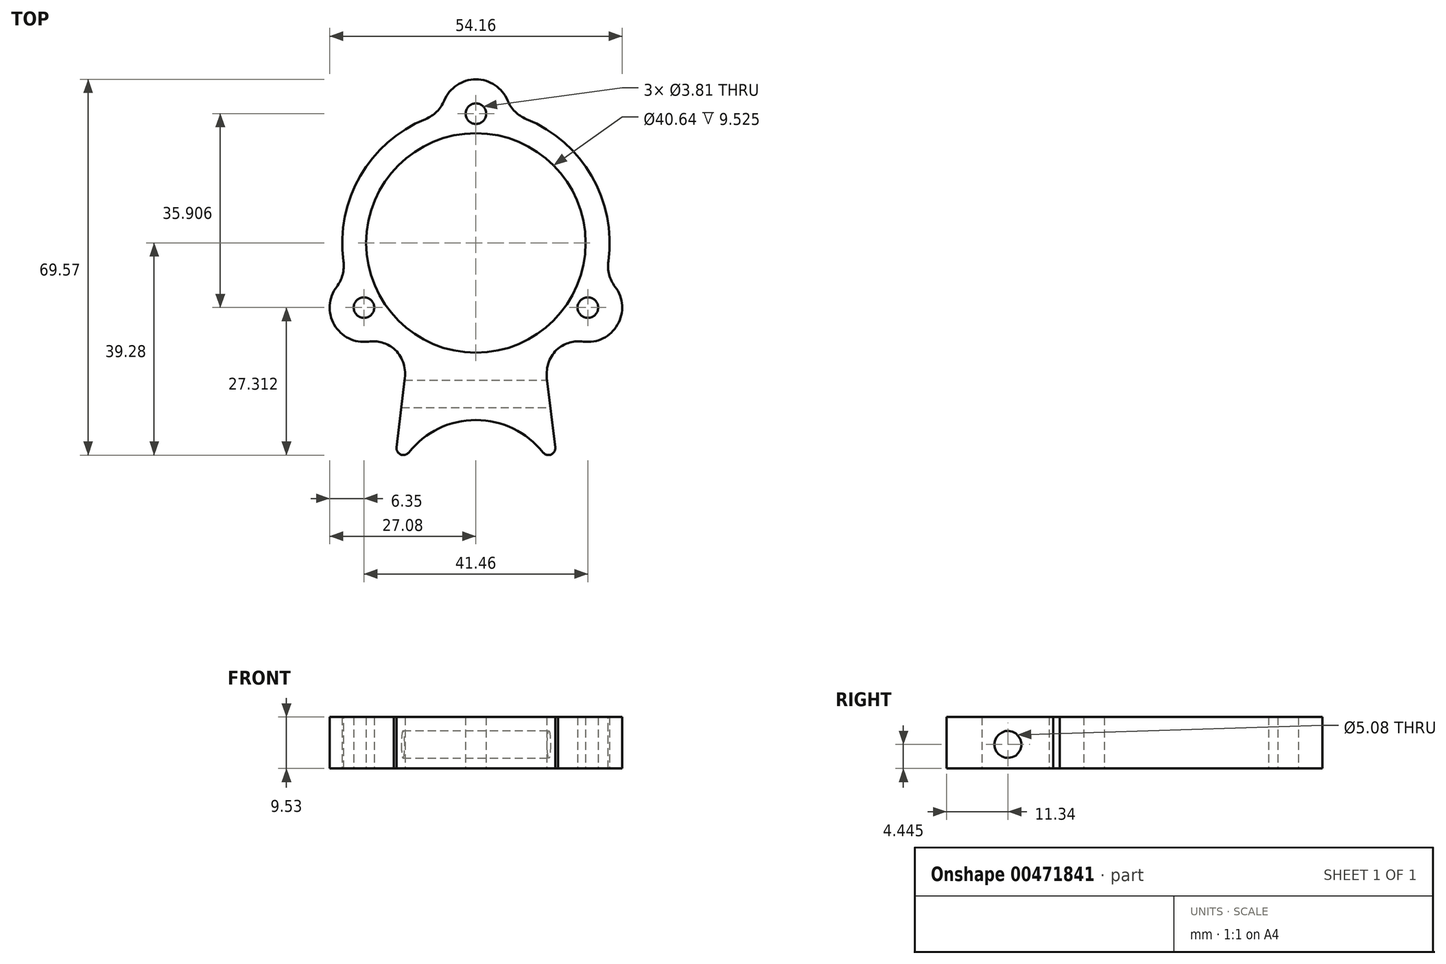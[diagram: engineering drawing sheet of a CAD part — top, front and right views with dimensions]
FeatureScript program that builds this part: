
annotation { "Feature Type Name" : "Feature", "Feature Type Description" : "" }
export const myFeature = defineFeature(function(context is Context, id is Id, definition is map)
    precondition{}
    {
        {
            var Q0;
            Q0=qCreatedBy(makeId("Top.planeOp"),FACE);
            var sketch = newSketch(context, id + "F0", { "sketchPlane" : qUnion([Q0])});
            skCircle(sketch, "E0", {"center": v(0, 0) * mm, "radius": 20.32 * mm});
            skCircle(sketch, "E1", {"center": v(0, 0) * mm, "radius": 24.77 * mm});
            skLineSegment(sketch, "E2", {"start": v(0, 0) * mm, "end": v(0, 42.77) * mm, "construction": true});
            skLineSegment(sketch, "E3", {"start": v(0, 0) * mm, "end": v(-43.71, -25.24) * mm, "construction": true});
            skLineSegment(sketch, "E4", {"start": v(0, 0) * mm, "end": v(46.9, -27.08) * mm, "construction": true});
            skLineSegment(sketch, "E5", {"start": v(-6.35, 2.16) * mm, "end": v(-6.35, 48.97) * mm, "construction": true});
            skLineSegment(sketch, "E6.MirrorCS", {"start": v(6.35, 2.16) * mm, "end": v(6.35, 48.97) * mm, "construction": true});
            skLineSegment(sketch, "E7", {"start": v(-11.23, 0.85) * mm, "end": v(-48.99, -20.95) * mm, "construction": true});
            skLineSegment(sketch, "E8.MirrorCS", {"start": v(-4.88, -10.15) * mm, "end": v(-42.64, -31.95) * mm, "construction": true});
            skLineSegment(sketch, "E9", {"start": v(0.14, -7.41) * mm, "end": v(38.48, -29.55) * mm, "construction": true});
            skLineSegment(sketch, "E10.MirrorCS", {"start": v(6.49, 3.59) * mm, "end": v(44.83, -18.55) * mm, "construction": true});
            skArc(sketch, "E11", {"start": v(6.35, 23.94) * mm, "mid": v(0, 30.29) * mm, "end": v(-6.35, 23.94) * mm});
            skArc(sketch, "E12", {"start": v(-23.9, -6.47) * mm, "mid": v(-26.23, -15.14) * mm, "end": v(-17.56, -17.47) * mm});
            skArc(sketch, "E13", {"start": v(17.56, -17.47) * mm, "mid": v(26.23, -15.14) * mm, "end": v(23.9, -6.47) * mm});
            skCircle(sketch, "E14", {"center": v(0, 23.94) * mm, "radius": 1.9 * mm});
            skCircle(sketch, "E15", {"center": v(-20.73, -11.97) * mm, "radius": 1.9 * mm});
            skCircle(sketch, "E16", {"center": v(20.73, -11.97) * mm, "radius": 1.9 * mm});
            skLineSegment(sketch, "E17", {"start": v(-12.7, -21.26) * mm, "end": v(-15.75, -46.66) * mm});
            skLineSegment(sketch, "E18.MirrorCS", {"start": v(12.7, -21.26) * mm, "end": v(15.75, -46.66) * mm});
            skArc(sketch, "E19", {"start": v(15.75, -46.66) * mm, "mid": v(0, -32.79) * mm, "end": v(-15.75, -46.66) * mm});
            skSolve(sketch);
        }
        {
            var Q0;
            Q0=makeQuery(id+"F0.imprint","IMPRINT",FACE,{"disambiguationData":[TD([[makeQuery(id+"F0.imprint","IMPRINT",EDGE,{"derivedFrom":sQuery(id+"F0.wireOp",EDGE,"E0")}),-1.0]])]});
            var Q1;
            {var subQ0=sQuery(id+"F0.wireOp",EDGE,"E12");Q1=makeQuery(id+"F0.imprint","IMPRINT",FACE,{"disambiguationData":[TD([[makeQuery(id+"F0.imprint","IMPRINT",EDGE,{"derivedFrom":subQ0}),1.0]])]});}
            var Q2;
            {var subQ0=sQuery(id+"F0.wireOp",EDGE,"E11");Q2=makeQuery(id+"F0.imprint","IMPRINT",FACE,{"disambiguationData":[TD([[makeQuery(id+"F0.imprint","IMPRINT",EDGE,{"derivedFrom":subQ0}),1.0]])]});}
            var Q3;
            {var subQ0=sQuery(id+"F0.wireOp",EDGE,"E13");Q3=makeQuery(id+"F0.imprint","IMPRINT",FACE,{"disambiguationData":[TD([[makeQuery(id+"F0.imprint","IMPRINT",EDGE,{"derivedFrom":subQ0}),1.0]])]});}
            var Q4;
            {var subQ0=sQuery(id+"F0.wireOp",EDGE,"E17");Q4=makeQuery(id+"F0.imprint","IMPRINT",FACE,{"disambiguationData":[TD([[makeQuery(id+"F0.imprint","IMPRINT",EDGE,{"derivedFrom":subQ0}),1.0]])]});}
            extrude(context, id + "F1", {"entities" : qUnion([Q0, Q1, Q2, Q3, Q4]), "depth" : 9.52 * mm});
        }
        {
            var Q0;
            {var subQ0=sQuery(id+"F0.wireOp",EDGE,"E11");var subQ1=sQuery(id+"F0.wireOp",EDGE,"E1");Q0=makeQuery(id+"F1.opExtrude","SWEPT_EDGE",EDGE,{"disambiguationData":[OSD([subQ1,subQ0]),TDD([makeQuery(id+"F0.imprint","INTERSECT",VERTEX,{"disambiguationData":[OD(1.0)],"derivedFrom":[subQ1,subQ0]})])]});}
            var Q1;
            {var subQ0=sQuery(id+"F0.wireOp",EDGE,"E12");var subQ1=sQuery(id+"F0.wireOp",EDGE,"E1");Q1=makeQuery(id+"F1.opExtrude","SWEPT_EDGE",EDGE,{"disambiguationData":[OSD([subQ1,subQ0]),TDD([makeQuery(id+"F0.imprint","INTERSECT",VERTEX,{"disambiguationData":[OD(0.0)],"derivedFrom":[subQ1,subQ0]})])]});}
            var Q2;
            {var subQ0=sQuery(id+"F0.wireOp",EDGE,"E12");var subQ1=sQuery(id+"F0.wireOp",EDGE,"E1");Q2=makeQuery(id+"F1.opExtrude","SWEPT_EDGE",EDGE,{"disambiguationData":[OSD([subQ1,subQ0]),TDD([makeQuery(id+"F0.imprint","INTERSECT",VERTEX,{"disambiguationData":[OD(1.0)],"derivedFrom":[subQ1,subQ0]})])]});}
            var Q3;
            {var subQ0=sQuery(id+"F0.wireOp",EDGE,"E13");var subQ1=sQuery(id+"F0.wireOp",EDGE,"E1");Q3=makeQuery(id+"F1.opExtrude","SWEPT_EDGE",EDGE,{"disambiguationData":[OSD([subQ1,subQ0]),TDD([makeQuery(id+"F0.imprint","INTERSECT",VERTEX,{"disambiguationData":[OD(0.0)],"derivedFrom":[subQ1,subQ0]})])]});}
            var Q4;
            {var subQ0=sQuery(id+"F0.wireOp",EDGE,"E13");var subQ1=sQuery(id+"F0.wireOp",EDGE,"E1");Q4=makeQuery(id+"F1.opExtrude","SWEPT_EDGE",EDGE,{"disambiguationData":[OSD([subQ1,subQ0]),TDD([makeQuery(id+"F0.imprint","INTERSECT",VERTEX,{"disambiguationData":[OD(1.0)],"derivedFrom":[subQ1,subQ0]})])]});}
            var Q5;
            {var subQ0=sQuery(id+"F0.wireOp",EDGE,"E11");var subQ1=sQuery(id+"F0.wireOp",EDGE,"E1");Q5=makeQuery(id+"F1.opExtrude","SWEPT_EDGE",EDGE,{"disambiguationData":[OSD([subQ1,subQ0]),TDD([makeQuery(id+"F0.imprint","INTERSECT",VERTEX,{"disambiguationData":[OD(0.0)],"derivedFrom":[subQ1,subQ0]})])]});}
            fillet(context, id + "F2", {"entities" : qUnion([Q0, Q1, Q2, Q3, Q4, Q5]), "radius" : 6.35 * mm, "tangentPropagation" : true, "allowEdgeOverflow" : false});
        }
        {
            var Q0;
            Q0=makeQuery(id+"F1.opExtrude","SWEPT_EDGE",EDGE,{"disambiguationData":[OSD([sQuery(id+"F0.wireOp",EDGE,"E1"),sQuery(id+"F0.wireOp",EDGE,"E17")])]});
            var Q1;
            Q1=makeQuery(id+"F1.opExtrude","SWEPT_EDGE",EDGE,{"disambiguationData":[OSD([sQuery(id+"F0.wireOp",EDGE,"E1"),sQuery(id+"F0.wireOp",EDGE,"E18.MirrorCS")])]});
            fillet(context, id + "F3", {"entities" : qUnion([Q0, Q1]), "radius" : 6.35 * mm, "tangentPropagation" : true, "allowEdgeOverflow" : false});
        }
        {
            var Q0;
            Q0=makeQuery(id+"F1.opExtrude","SWEPT_EDGE",EDGE,{"disambiguationData":[OSD([sQuery(id+"F0.wireOp",EDGE,"E17"),sQuery(id+"F0.wireOp",EDGE,"E19")])]});
            var Q1;
            Q1=makeQuery(id+"F1.opExtrude","SWEPT_EDGE",EDGE,{"disambiguationData":[OSD([sQuery(id+"F0.wireOp",EDGE,"E18.MirrorCS"),sQuery(id+"F0.wireOp",EDGE,"E19")])]});
            fillet(context, id + "F4", {"entities" : qUnion([Q0, Q1]), "radius" : 1.27 * mm, "tangentPropagation" : true, "allowEdgeOverflow" : false});
        }
        {
            var Q0;
            Q0=qCreatedBy(makeId("Right.planeOp"),FACE);
            var sketch = newSketch(context, id + "F5", { "sketchPlane" : qUnion([Q0])});
            skCircle(sketch, "E20", {"center": v(-27.94, 4.44) * mm, "radius": 2.54 * mm});
            skSolve(sketch);
        }
        {
            var Q0;
            Q0=makeQuery(id+"F5.imprint","IMPRINT",FACE,{"disambiguationData":[TD([[makeQuery(id+"F5.imprint","IMPRINT",EDGE,{"derivedFrom":sQuery(id+"F5.wireOp",EDGE,"E20")}),1.0]])]});
            extrude(context, id + "F6", {"entities" : qUnion([Q0]), "operationType" : NewBodyOperationType.REMOVE, "endBound" : BoundingType.SYMMETRIC, "oppositeDirection" : true, "depth" : 76.2 * mm});
        }
    });
